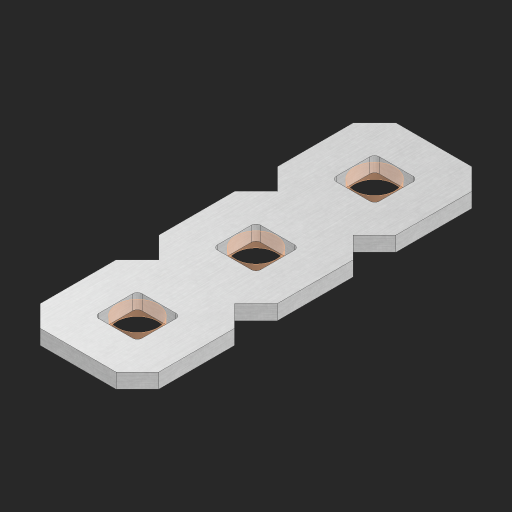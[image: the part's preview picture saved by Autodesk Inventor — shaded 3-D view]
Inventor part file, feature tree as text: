
AUTODESK INVENTOR PART (.ipt)
format: ipt  version: 2023 (Build 270158000, 158)  size: 310,272 bytes
history: native  units: in
note: dims shown in document units (in); Inventor stores cm internally (conversion verified against a paired STEP export)
features: other x4, sketch x2, extrude x2, pattern_linear x1
ambient origin geometry x8: Origin, YZ Plane, XZ Plane, XY Plane, X Axis, Y Axis, Z Axis, Center Point
bodies: Solid1 (feature_tree), Body (feature_tree)
feature tree (9):
  pattern_linear  "Rectangular Pattern1"  Spacing1=0.09in  [1 undecoded]
  sketch  "Sketch1"  dims[d1=0.5in]
  sketch  "Sketch2"  dims[d2=0.182in d3=0.09in d4=0.09in d5=0.09in d6=0.09in d7=0.09in d8=0.09in d9=0.09in d10=0.09in d11=0.02in d13=0.0in d14=0.172in d15=0.0625in d16=0.0in d19=0.5in d22=0.5in]
  other  "Srf1"
  other  "Srf126"
  other  "Srf127"
  other  "Circle"
  extrude  "ExtrusionSrf126"  Depth=0.09in
  extrude  "ExtrusionSrf127"  Depth=0.09in
note: 1 required parameter value undecoded (feature->parameter linkage not recoverable at this tier; creation-order binding heuristic only, values carry confidence <= 0.55)
